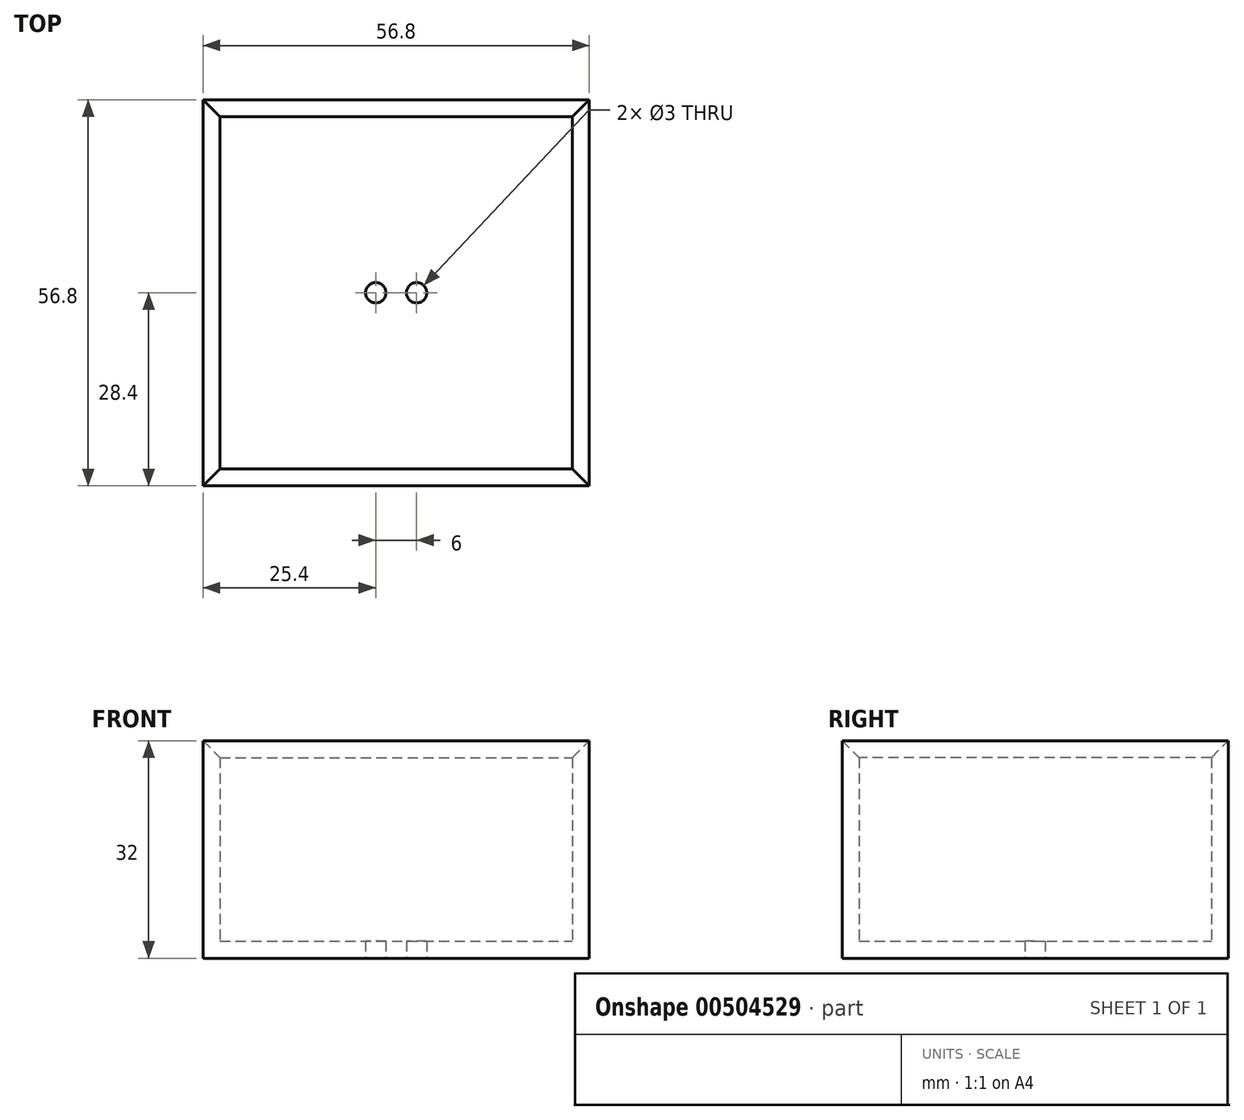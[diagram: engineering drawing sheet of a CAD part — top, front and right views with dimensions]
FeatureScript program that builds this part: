
annotation { "Feature Type Name" : "Feature", "Feature Type Description" : "" }
export const myFeature = defineFeature(function(context is Context, id is Id, definition is map)
    precondition{}
    {
        {
            var Q0;
            Q0=qCreatedBy(makeId("Top.planeOp"),FACE);
            var sketch = newSketch(context, id + "F0", { "sketchPlane" : qUnion([Q0])});
            skLineSegment(sketch, "E0.bottom", {"start": v(0, 0) * mm, "end": v(56.8, 0) * mm});
            skLineSegment(sketch, "E0.top", {"start": v(0, 56.8) * mm, "end": v(56.8, 56.8) * mm});
            skLineSegment(sketch, "E0.left", {"start": v(0, 0) * mm, "end": v(0, 56.8) * mm});
            skLineSegment(sketch, "E0.right", {"start": v(56.8, 0) * mm, "end": v(56.8, 56.8) * mm});
            skSolve(sketch);
        }
        {
            var Q0;
            Q0 = qSketchRegion(id + "F0", true);
            extrude(context, id + "F1", {"entities" : qUnion([Q0]), "depth" : 32 * mm});
        }
        {
            var Q0;
            Q0=makeQuery(id+"F1.opExtrude","CAP_FACE",FACE,{"disambiguationData":[OSD([sQuery(id+"F0.wireOp",EDGE,"E0.bottom"),sQuery(id+"F0.wireOp",EDGE,"E0.top"),sQuery(id+"F0.wireOp",EDGE,"E0.left"),sQuery(id+"F0.wireOp",EDGE,"E0.right")])],"isStart":false});
            shell(context, id + "F2", {"entities" : qUnion([Q0]), "thickness" : 2.5 * mm});
        }
        {
            var Q0;
            Q0=makeQuery(id+"F1.opExtrude","CAP_FACE",FACE,{"disambiguationData":[OSD([sQuery(id+"F0.wireOp",EDGE,"E0.bottom"),sQuery(id+"F0.wireOp",EDGE,"E0.top"),sQuery(id+"F0.wireOp",EDGE,"E0.left"),sQuery(id+"F0.wireOp",EDGE,"E0.right")])],"isStart":true});
            var sketch = newSketch(context, id + "F3", { "sketchPlane" : qUnion([Q0])});
            skPoint(sketch, "E1.startSnap0", {"position": v(28.4, 0) * mm});
            skPoint(sketch, "E1.startSnap1", {"position": v(0, -28.4) * mm});
            skCircle(sketch, "E2", {"center": v(31.4, -28.4) * mm, "radius": 1.5 * mm});
            skCircle(sketch, "E3", {"center": v(25.4, -28.4) * mm, "radius": 1.5 * mm});
            skSolve(sketch);
        }
        {
            var Q0;
            Q0=makeQuery(id+"F3.imprint","IMPRINT",FACE,{"disambiguationData":[TD([[makeQuery(id+"F3.imprint","IMPRINT",EDGE,{"derivedFrom":sQuery(id+"F3.wireOp",EDGE,"E3")}),1.0]])]});
            var Q1;
            Q1=makeQuery(id+"F3.imprint","IMPRINT",FACE,{"disambiguationData":[TD([[makeQuery(id+"F3.imprint","IMPRINT",EDGE,{"derivedFrom":sQuery(id+"F3.wireOp",EDGE,"E2")}),1.0]])]});
            extrude(context, id + "F4", {"entities" : qUnion([Q0, Q1]), "operationType" : NewBodyOperationType.REMOVE, "endBound" : BoundingType.UP_TO_NEXT, "oppositeDirection" : true, "depth" : 25 * mm});
        }
        {
            var Q0;
            {var subQ0=sQuery(id+"F0.wireOp",EDGE,"E0.left");Q0=makeQuery(id+"F2.opShell","OFFSET_EDGE",EDGE,{"disambiguationData":[OSD([subQ0]),TDD([makeQuery(id+"F1.opExtrude","CAP_EDGE",EDGE,{"disambiguationData":[OSD([subQ0])],"isStart":false})])]});}
            var Q1;
            {var subQ0=sQuery(id+"F0.wireOp",EDGE,"E0.bottom");Q1=makeQuery(id+"F2.opShell","OFFSET_EDGE",EDGE,{"disambiguationData":[OSD([subQ0]),TDD([makeQuery(id+"F1.opExtrude","CAP_EDGE",EDGE,{"disambiguationData":[OSD([subQ0])],"isStart":false})])]});}
            var Q2;
            {var subQ0=sQuery(id+"F0.wireOp",EDGE,"E0.right");Q2=makeQuery(id+"F2.opShell","OFFSET_EDGE",EDGE,{"disambiguationData":[OSD([subQ0]),TDD([makeQuery(id+"F1.opExtrude","CAP_EDGE",EDGE,{"disambiguationData":[OSD([subQ0])],"isStart":false})])]});}
            var Q3;
            {var subQ0=sQuery(id+"F0.wireOp",EDGE,"E0.top");Q3=makeQuery(id+"F2.opShell","OFFSET_EDGE",EDGE,{"disambiguationData":[OSD([subQ0]),TDD([makeQuery(id+"F1.opExtrude","CAP_EDGE",EDGE,{"disambiguationData":[OSD([subQ0])],"isStart":false})])]});}
            chamfer(context, id + "F5", {"entities" : qUnion([Q0, Q1, Q2, Q3]), "width" : 2.5 * mm, "tangentPropagation" : true});
        }
    });
